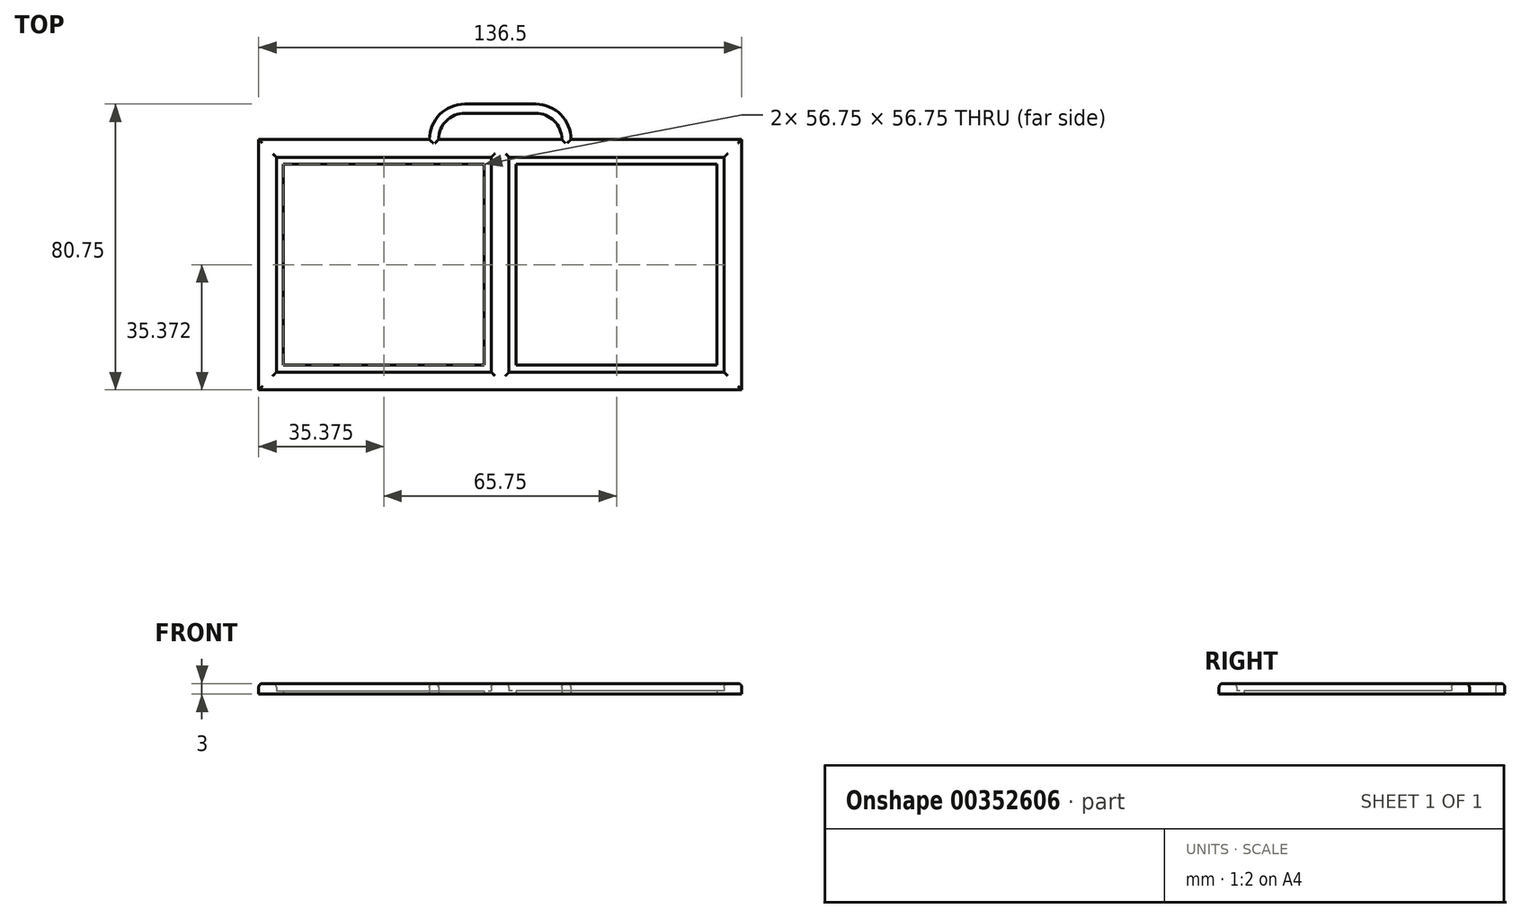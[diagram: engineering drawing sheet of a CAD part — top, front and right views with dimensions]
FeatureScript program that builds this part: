
annotation { "Feature Type Name" : "Feature", "Feature Type Description" : "" }
export const myFeature = defineFeature(function(context is Context, id is Id, definition is map)
    precondition{}
    {
        {
            var Q0;
            Q0=qCreatedBy(makeId("Top.planeOp"),FACE);
            var sketch = newSketch(context, id + "F0", { "sketchPlane" : qUnion([Q0])});
            skLineSegment(sketch, "E0.bottom", {"start": v(-63.25, 26.55) * mm, "end": v(-2.5, 26.55) * mm});
            skLineSegment(sketch, "E0.top", {"start": v(-63.25, -34.2) * mm, "end": v(-2.5, -34.2) * mm});
            skLineSegment(sketch, "E0.left", {"start": v(-63.25, 26.55) * mm, "end": v(-63.25, -34.2) * mm});
            skLineSegment(sketch, "E0.right", {"start": v(-2.5, 26.55) * mm, "end": v(-2.5, -34.2) * mm});
            skPoint(sketch, "E1", {"position": v(-2.5, 26.55) * mm});
            skPoint(sketch, "E2", {"position": v(-2.5, 31.55) * mm});
            skPoint(sketch, "E3", {"position": v(-2.5, -34.2) * mm});
            skPoint(sketch, "E4", {"position": v(-2.5, -39.2) * mm});
            skPoint(sketch, "E5", {"position": v(-63.25, -39.2) * mm});
            skPoint(sketch, "E6", {"position": v(-63.25, 31.55) * mm});
            skPoint(sketch, "E7", {"position": v(-63.25, 26.55) * mm});
            skPoint(sketch, "E8", {"position": v(-68.25, 26.55) * mm});
            skPoint(sketch, "E9", {"position": v(-68.25, 31.55) * mm});
            skPoint(sketch, "E10", {"position": v(0, -39.2) * mm});
            skLineSegment(sketch, "E11.bottom", {"start": v(-68.25, 31.55) * mm, "end": v(0, 31.55) * mm});
            skLineSegment(sketch, "E11.top", {"start": v(-68.25, -39.2) * mm, "end": v(0, -39.2) * mm});
            skLineSegment(sketch, "E11.left", {"start": v(-68.25, 31.55) * mm, "end": v(-68.25, -39.2) * mm});
            skLineSegment(sketch, "E11.right", {"start": v(0, 31.55) * mm, "end": v(0, -39.2) * mm});
            skPoint(sketch, "E12", {"position": v(-34.12, 31.55) * mm});
            skPoint(sketch, "E13", {"position": v(-34.12, 41.55) * mm});
            skLineSegment(sketch, "E14", {"start": v(-34.12, 41.55) * mm, "end": v(-34.12, 31.55) * mm});
            skPoint(sketch, "E15", {"position": v(-34.12, 36.55) * mm});
            skPoint(sketch, "E16", {"position": v(-34.12, 38.98) * mm});
            skPoint(sketch, "E17", {"position": v(-61.25, 26.55) * mm});
            skPoint(sketch, "E18", {"position": v(-63.25, 24.55) * mm});
            skPoint(sketch, "E19", {"position": v(-61.25, 24.55) * mm});
            skPoint(sketch, "E20", {"position": v(-2.5, -32.2) * mm});
            skPoint(sketch, "E21", {"position": v(-4.5, -34.2) * mm});
            skPoint(sketch, "E22", {"position": v(-4.5, -32.2) * mm});
            skLineSegment(sketch, "E23.bottom", {"start": v(-61.25, 24.55) * mm, "end": v(-4.5, 24.55) * mm});
            skLineSegment(sketch, "E23.top", {"start": v(-61.25, -32.2) * mm, "end": v(-4.5, -32.2) * mm});
            skLineSegment(sketch, "E23.left", {"start": v(-61.25, 24.55) * mm, "end": v(-61.25, -32.2) * mm});
            skLineSegment(sketch, "E23.right", {"start": v(-4.5, 24.55) * mm, "end": v(-4.5, -32.2) * mm});
            skPoint(sketch, "E24", {"position": v(0, 38.98) * mm});
            skPoint(sketch, "E25", {"position": v(0, 41.55) * mm});
            skPoint(sketch, "E26", {"position": v(-10, 41.55) * mm});
            skPoint(sketch, "E27", {"position": v(-10, 38.98) * mm});
            skLineSegment(sketch, "E28", {"start": v(0, 41.55) * mm, "end": v(-10, 41.55) * mm});
            skLineSegment(sketch, "E29", {"start": v(0, 38.98) * mm, "end": v(-10, 38.98) * mm});
            skArc(sketch, "E30", {"start": v(-10, 38.98) * mm, "mid": v(-15.25, 36.8) * mm, "end": v(-17.43, 31.55) * mm});
            skArc(sketch, "E31", {"start": v(-10, 41.55) * mm, "mid": v(-17.07, 38.62) * mm, "end": v(-20, 31.55) * mm});
            skLineSegment(sketch, "E32", {"start": v(-17.43, 31.55) * mm, "end": v(-17.43, 26.55) * mm});
            skLineSegment(sketch, "E33", {"start": v(-20, 31.55) * mm, "end": v(-20, 26.55) * mm});
            skLineSegment(sketch, "E34", {"start": v(0, 38.98) * mm, "end": v(0, 41.55) * mm});
            skSolve(sketch);
        }
        {
            var Q0;
            Q0=makeQuery(id+"F0.imprint","IMPRINT",FACE,{"disambiguationData":[TD([[makeQuery(id+"F0.imprint","IMPRINT",EDGE,{"derivedFrom":sQuery(id+"F0.wireOp",EDGE,"E0.top")}),-1.0]])]});
            var Q1;
            {var subQ0=sQuery(id+"F0.wireOp",EDGE,"323iFSkM-69Tl-kqoX-bfbl-zxdwPlZIsCMZ");var subQ1=sQuery(id+"F0.wireOp",EDGE,"E0.bottom");var subQ2=makeQuery(id+"F0.imprint","INTERSECT",VERTEX,{"disambiguationData":[OD(0.0)],"derivedFrom":[subQ1,subQ0]});Q1=makeQuery(id+"F0.imprint","IMPRINT",FACE,{"disambiguationData":[TD([[makeQuery(id+"F0.imprint","IMPRINT",EDGE,{"disambiguationData":[TD([[subQ2,-1.0]])],"derivedFrom":subQ1}),1.0]])]});}
            var Q2;
            {var subQ0=sQuery(id+"F0.wireOp",EDGE,"S2f47POQ-odG1-F0nU-moLb-DiT50xx8mqJj");var subQ1=sQuery(id+"F0.wireOp",EDGE,"E0.bottom");var subQ2=makeQuery(id+"F0.imprint","INTERSECT",VERTEX,{"disambiguationData":[OD(1.0)],"derivedFrom":[subQ1,subQ0]});Q2=makeQuery(id+"F0.imprint","IMPRINT",FACE,{"disambiguationData":[TD([[makeQuery(id+"F0.imprint","IMPRINT",EDGE,{"disambiguationData":[TD([[subQ2,-1.0]])],"derivedFrom":subQ1}),1.0]])]});}
            var Q3;
            {var subQ0=sQuery(id+"F0.wireOp",EDGE,"323iFSkM-69Tl-kqoX-bfbl-zxdwPlZIsCMZ");var subQ1=sQuery(id+"F0.wireOp",EDGE,"E11.bottom");var subQ2=makeQuery(id+"F0.imprint","INTERSECT",VERTEX,{"disambiguationData":[OD(1.0)],"derivedFrom":[subQ1,subQ0]});Q3=makeQuery(id+"F0.imprint","IMPRINT",FACE,{"disambiguationData":[TD([[makeQuery(id+"F0.imprint","IMPRINT",EDGE,{"disambiguationData":[TD([[subQ2,1.0]])],"derivedFrom":subQ1}),1.0]])]});}
            var Q4;
            {var subQ0=sQuery(id+"F0.wireOp",EDGE,"S2f47POQ-odG1-F0nU-moLb-DiT50xx8mqJj");var subQ1=sQuery(id+"F0.wireOp",EDGE,"E0.bottom");var subQ2=makeQuery(id+"F0.imprint","INTERSECT",VERTEX,{"disambiguationData":[OD(0.0)],"derivedFrom":[subQ1,subQ0]});Q4=makeQuery(id+"F0.imprint","IMPRINT",FACE,{"disambiguationData":[TD([[makeQuery(id+"F0.imprint","IMPRINT",EDGE,{"disambiguationData":[TD([[subQ2,-1.0]])],"derivedFrom":subQ1}),1.0]])]});}
            var Q5;
            {var subQ0=sQuery(id+"F0.wireOp",EDGE,"RwKeYdOv-RQ1C-EBcZ-qULq-cMKYxm2aIbZM");var subQ1=sQuery(id+"F0.wireOp",EDGE,"E0.right");var subQ2=makeQuery(id+"F0.imprint","INTERSECT",VERTEX,{"derivedFrom":[subQ1,subQ0]});Q5=makeQuery(id+"F0.imprint","IMPRINT",FACE,{"disambiguationData":[TD([[makeQuery(id+"F0.imprint","IMPRINT",EDGE,{"disambiguationData":[TD([[subQ2,-1.0]])],"derivedFrom":subQ1}),1.0]])]});}
            var Q6;
            {var subQ6=sQuery(id+"F0.wireOp",EDGE,"E0.bottom");var subQ8=sQuery(id+"F0.wireOp",EDGE,"E0.right");var subQ9=makeQuery(id+"F0.imprint","INTERSECT",VERTEX,{"derivedFrom":[subQ6,subQ8]});Q6=makeQuery(id+"F0.imprint","IMPRINT",FACE,{"disambiguationData":[TD([[makeQuery(id+"F0.imprint","IMPRINT",EDGE,{"disambiguationData":[TD([[subQ9,1.0]])],"derivedFrom":subQ6}),1.0]])]});}
            var Q7;
            {var subQ0=sQuery(id+"F0.wireOp",EDGE,"E32");Q7=makeQuery(id+"F0.imprint","IMPRINT",FACE,{"disambiguationData":[TD([[makeQuery(id+"F0.imprint","IMPRINT",EDGE,{"derivedFrom":subQ0}),-1.0]])]});}
            var Q8;
            Q8=makeQuery(id+"F0.imprint","IMPRINT",FACE,{"disambiguationData":[TD([[makeQuery(id+"F0.imprint","IMPRINT",EDGE,{"derivedFrom":sQuery(id+"F0.wireOp",EDGE,"E28")}),1.0]])]});
            extrude(context, id + "F1", {"entities" : qUnion([Q0, Q1, Q2, Q3, Q4, Q5, Q6, Q7, Q8]), "depth" : 3 * mm, "offsetDistance" : 25 * mm});
        }
        {
            var Q0;
            {var subQ0=sQuery(id+"F0.wireOp",EDGE,"S2f47POQ-odG1-F0nU-moLb-DiT50xx8mqJj");var subQ1=sQuery(id+"F0.wireOp",EDGE,"E0.bottom");var subQ2=makeQuery(id+"F0.imprint","INTERSECT",VERTEX,{"disambiguationData":[OD(0.0)],"derivedFrom":[subQ1,subQ0]});Q0=makeQuery(id+"F0.imprint","IMPRINT",FACE,{"disambiguationData":[TD([[makeQuery(id+"F0.imprint","IMPRINT",EDGE,{"disambiguationData":[TD([[subQ2,-1.0]])],"derivedFrom":subQ1}),-1.0]])]});}
            var Q1;
            {var subQ0=sQuery(id+"F0.wireOp",EDGE,"323iFSkM-69Tl-kqoX-bfbl-zxdwPlZIsCMZ");var subQ1=sQuery(id+"F0.wireOp",EDGE,"E0.bottom");var subQ2=makeQuery(id+"F0.imprint","INTERSECT",VERTEX,{"disambiguationData":[OD(0.0)],"derivedFrom":[subQ1,subQ0]});Q1=makeQuery(id+"F0.imprint","IMPRINT",FACE,{"disambiguationData":[TD([[makeQuery(id+"F0.imprint","IMPRINT",EDGE,{"disambiguationData":[TD([[subQ2,-1.0]])],"derivedFrom":subQ1}),-1.0]])]});}
            var Q2;
            {var subQ0=sQuery(id+"F0.wireOp",EDGE,"S2f47POQ-odG1-F0nU-moLb-DiT50xx8mqJj");var subQ1=sQuery(id+"F0.wireOp",EDGE,"E0.bottom");var subQ2=makeQuery(id+"F0.imprint","INTERSECT",VERTEX,{"disambiguationData":[OD(1.0)],"derivedFrom":[subQ1,subQ0]});Q2=makeQuery(id+"F0.imprint","IMPRINT",FACE,{"disambiguationData":[TD([[makeQuery(id+"F0.imprint","IMPRINT",EDGE,{"disambiguationData":[TD([[subQ2,-1.0]])],"derivedFrom":subQ1}),-1.0]])]});}
            var Q3;
            Q3=makeQuery(id+"F0.imprint","IMPRINT",FACE,{"disambiguationData":[TD([[makeQuery(id+"F0.imprint","IMPRINT",EDGE,{"derivedFrom":sQuery(id+"F0.wireOp",EDGE,"E0.top")}),1.0]])]});
            var Q4;
            {var subQ3=sQuery(id+"F0.wireOp",EDGE,"oISM5f6R-s7pY-zFvx-TeqI-MK5FqsrAusou");var subQ10=sQuery(id+"F0.wireOp",EDGE,"E0.bottom");var subQ11=makeQuery(id+"F0.imprint","INTERSECT",VERTEX,{"derivedFrom":[subQ10,subQ3]});Q4=makeQuery(id+"F0.imprint","IMPRINT",FACE,{"disambiguationData":[TD([[makeQuery(id+"F0.imprint","IMPRINT",EDGE,{"disambiguationData":[TD([[subQ11,-1.0]])],"derivedFrom":subQ10}),-1.0]])]});}
            extrude(context, id + "F2", {"entities" : qUnion([Q0, Q1, Q2, Q3, Q4]), "operationType" : NewBodyOperationType.ADD, "depth" : 1 * mm});
        }
        {
            var Q0;
            Q0=makeQuery(id+"F1.opExtrude","CAP_EDGE",EDGE,{"disambiguationData":[OSD([sQuery(id+"F0.wireOp",EDGE,"E0.bottom")])],"isStart":false});
            var Q1;
            Q1=makeQuery(id+"F1.opExtrude","CAP_EDGE",EDGE,{"disambiguationData":[OSD([sQuery(id+"F0.wireOp",EDGE,"E0.left")])],"isStart":false});
            var Q2;
            Q2=makeQuery(id+"F1.opExtrude","CAP_EDGE",EDGE,{"disambiguationData":[OSD([sQuery(id+"F0.wireOp",EDGE,"E0.top")])],"isStart":false});
            var Q3;
            Q3=makeQuery(id+"F1.opExtrude","CAP_EDGE",EDGE,{"disambiguationData":[OSD([sQuery(id+"F0.wireOp",EDGE,"E0.right")])],"isStart":false});
            var Q4;
            {var subQ0=sQuery(id+"F0.wireOp",EDGE,"E11.bottom");var subQ1=makeQuery(id+"F0.imprint","IMPRINT",VERTEX,{"derivedFrom":subQ0});Q4=makeQuery(id+"F1.opExtrude","CAP_EDGE",EDGE,{"disambiguationData":[OSD([subQ0]),TDD([makeQuery(id+"F0.imprint","IMPRINT",EDGE,{"disambiguationData":[TD([[subQ1,1.0]])],"derivedFrom":subQ0}),makeQuery(id+"F0.imprint","IMPRINT",EDGE,{"disambiguationData":[TD([[subQ1,-1.0]])],"derivedFrom":subQ0})])],"isStart":false});}
            var Q5;
            Q5=makeQuery(id+"F1.opExtrude","CAP_EDGE",EDGE,{"disambiguationData":[OSD([sQuery(id+"F0.wireOp",EDGE,"E11.left")])],"isStart":false});
            var Q6;
            Q6=makeQuery(id+"F1.opExtrude","CAP_EDGE",EDGE,{"disambiguationData":[OSD([sQuery(id+"F0.wireOp",EDGE,"E11.top")])],"isStart":false});
            var Q7;
            Q7=makeQuery(id+"F1.opExtrude","CAP_EDGE",EDGE,{"disambiguationData":[OSD([sQuery(id+"F0.wireOp",EDGE,"oISM5f6R-s7pY-zFvx-TeqI-MK5FqsrAusou")])],"isStart":false});
            var Q8;
            Q8=makeQuery(id+"F1.opExtrude","CAP_EDGE",EDGE,{"disambiguationData":[OSD([sQuery(id+"F0.wireOp",EDGE,"RwKeYdOv-RQ1C-EBcZ-qULq-cMKYxm2aIbZM")])],"isStart":false});
            var Q9;
            {var subQ0=sQuery(id+"F0.wireOp",EDGE,"E11.bottom");Q9=makeQuery(id+"F1.opExtrude","CAP_EDGE",EDGE,{"disambiguationData":[OSD([subQ0]),TDD([makeQuery(id+"F0.imprint","IMPRINT",EDGE,{"disambiguationData":[TD([[makeQuery(id+"F0.imprint","INTERSECT",VERTEX,{"derivedFrom":[subQ0,sQuery(id+"F0.wireOp",EDGE,"RwKeYdOv-RQ1C-EBcZ-qULq-cMKYxm2aIbZM")]}),-1.0]])],"derivedFrom":subQ0})])],"isStart":false});}
            var Q10;
            {var subQ0=sQuery(id+"F0.wireOp",EDGE,"E11.bottom");Q10=makeQuery(id+"F1.opExtrude","CAP_EDGE",EDGE,{"disambiguationData":[OSD([subQ0]),TDD([makeQuery(id+"F0.imprint","IMPRINT",EDGE,{"disambiguationData":[TD([[makeQuery(id+"F0.imprint","INTERSECT",VERTEX,{"derivedFrom":[subQ0,sQuery(id+"F0.wireOp",EDGE,"E11.right")]}),1.0]])],"derivedFrom":subQ0})])],"isStart":false});}
            var Q11;
            Q11=makeQuery(id+"F1.opExtrude","CAP_EDGE",EDGE,{"disambiguationData":[OSD([sQuery(id+"F0.wireOp",EDGE,"E30")])],"isStart":false});
            var Q12;
            Q12=makeQuery(id+"F1.opExtrude","CAP_EDGE",EDGE,{"disambiguationData":[OSD([sQuery(id+"F0.wireOp",EDGE,"E31")])],"isStart":false});
            fillet(context, id + "F3", {"entities" : qUnion([Q0, Q1, Q2, Q3, Q4, Q5, Q6, Q7, Q8, Q9, Q10, Q11, Q12]), "radius" : 1 * mm, "tangentPropagation" : true, "allowEdgeOverflow" : false});
        }
        {
            var Q0;
            Q0=makeQuery(id+"F1.opExtrude","SWEPT_BODY",BODY,{"disambiguationData":[OSD([sQuery(id+"F0.wireOp",EDGE,"E0.bottom"),sQuery(id+"F0.wireOp",EDGE,"E0.top"),sQuery(id+"F0.wireOp",EDGE,"E0.left"),sQuery(id+"F0.wireOp",EDGE,"E0.right"),sQuery(id+"F0.wireOp",EDGE,"E11.bottom"),sQuery(id+"F0.wireOp",EDGE,"E11.top"),sQuery(id+"F0.wireOp",EDGE,"E11.left"),sQuery(id+"F0.wireOp",EDGE,"E11.right"),sQuery(id+"F0.wireOp",EDGE,"323iFSkM-69Tl-kqoX-bfbl-zxdwPlZIsCMZ"),sQuery(id+"F0.wireOp",EDGE,"S2f47POQ-odG1-F0nU-moLb-DiT50xx8mqJj")])]});
            var Q1;
            Q1=qCreatedBy(makeId("Right.planeOp"),FACE);
            mirror(context, id + "F4", {"operationType" : NewBodyOperationType.ADD, "entities" : qUnion([Q0]), "mirrorPlane" : qUnion([Q1])});
        }
    });
